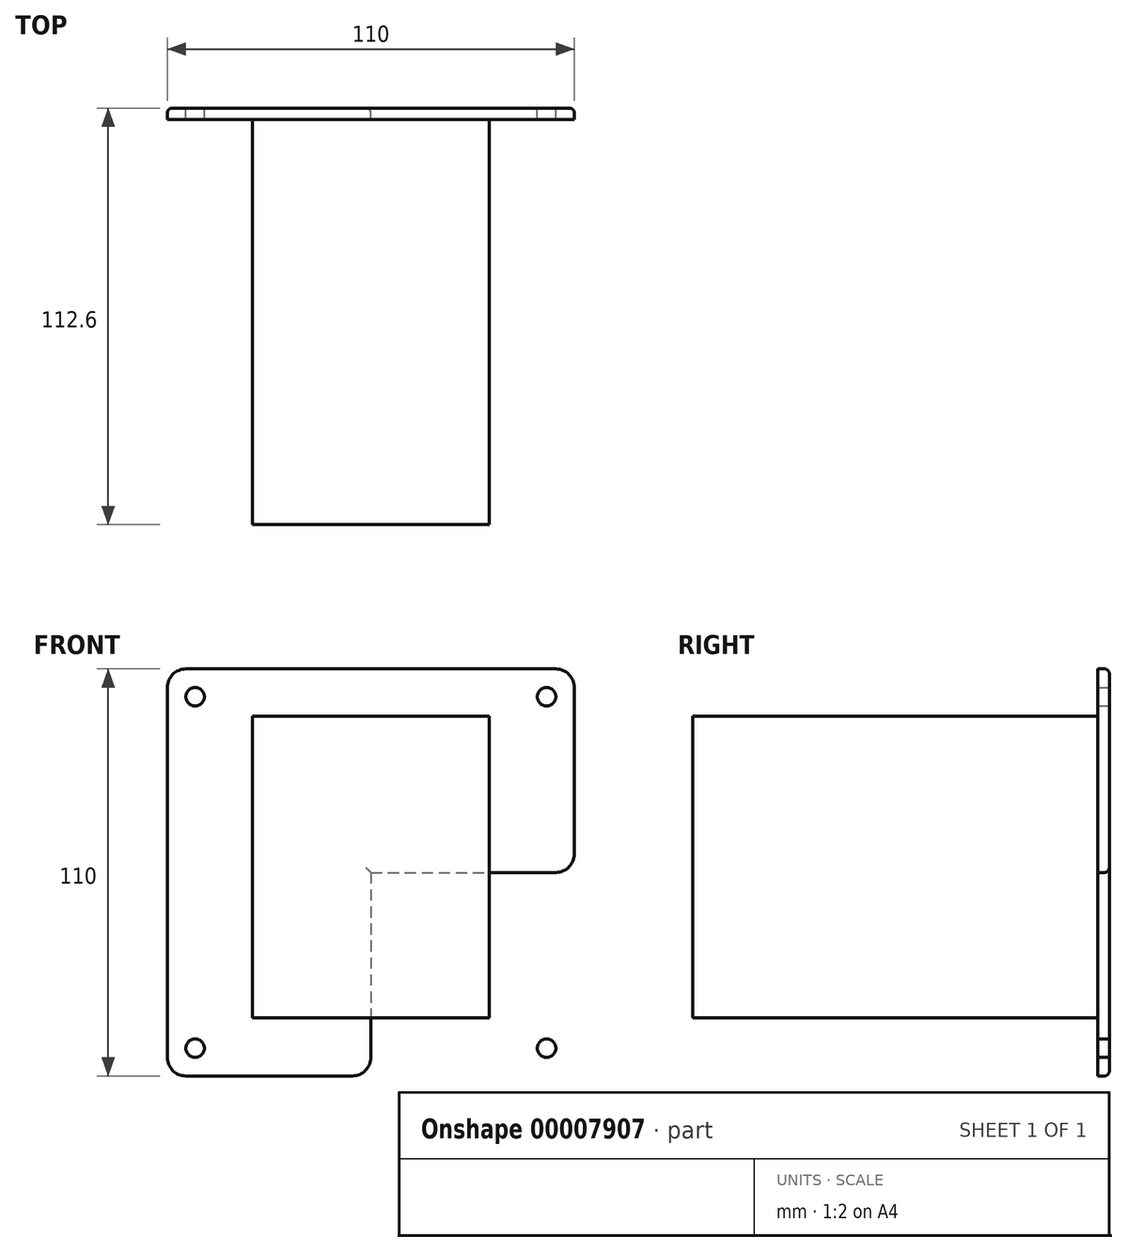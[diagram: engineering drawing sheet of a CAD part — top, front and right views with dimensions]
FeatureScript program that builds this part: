
annotation { "Feature Type Name" : "Feature", "Feature Type Description" : "" }
export const myFeature = defineFeature(function(context is Context, id is Id, definition is map)
    precondition{}
    {
        {
            var Q0;
            Q0=qCreatedBy(makeId("Front.planeOp"),FACE);
            var sketch = newSketch(context, id + "F0", { "sketchPlane" : qUnion([Q0])});
            skLineSegment(sketch, "E0.bottom", {"start": v(-55, 53.55) * mm, "end": v(55, 53.55) * mm});
            skLineSegment(sketch, "E0.top", {"start": v(-55, -56.45) * mm, "end": v(55, -56.45) * mm});
            skLineSegment(sketch, "E0.left", {"start": v(-55, 53.55) * mm, "end": v(-55, -56.45) * mm});
            skLineSegment(sketch, "E0.right", {"start": v(55, 53.55) * mm, "end": v(55, -56.45) * mm});
            skCircle(sketch, "E1", {"center": v(-47.5, 46.05) * mm, "radius": 2.5 * mm});
            skCircle(sketch, "E2", {"center": v(-47.5, -48.95) * mm, "radius": 2.5 * mm});
            skPoint(sketch, "E3", {"position": v(84.62, 69.4) * mm});
            skCircle(sketch, "E4.0.MirrorC", {"center": v(47.5, -48.95) * mm, "radius": 2.5 * mm});
            skCircle(sketch, "E4.1.MirrorC", {"center": v(47.5, 46.05) * mm, "radius": 2.5 * mm});
            skPoint(sketch, "E5", {"position": v(0, 53.55) * mm});
            skPoint(sketch, "E6", {"position": v(0, -56.45) * mm});
            skPoint(sketch, "E7", {"position": v(-55, -1.45) * mm});
            skPoint(sketch, "E8", {"position": v(55, -1.45) * mm});
            skLineSegment(sketch, "E9", {"start": v(0, 53.55) * mm, "end": v(0, -56.45) * mm});
            skLineSegment(sketch, "E10", {"start": v(-55, -1.45) * mm, "end": v(55, -1.45) * mm});
            skSolve(sketch);
        }
        {
            var Q0;
            Q0=makeQuery(id+"F0.imprint","IMPRINT",FACE,{"disambiguationData":[TD([[makeQuery(id+"F0.imprint","IMPRINT",EDGE,{"derivedFrom":sQuery(id+"F0.wireOp",EDGE,"E0.bottom")}),-1.0]])]});
            var Q1;
            Q1=makeQuery(id+"F0.imprint","IMPRINT",FACE,{"disambiguationData":[TD([[makeQuery(id+"F0.imprint","IMPRINT",EDGE,{"derivedFrom":sQuery(id+"F0.wireOp",EDGE,"E2")}),-1.0]])]});
            var Q2;
            Q2=makeQuery(id+"F0.imprint","IMPRINT",FACE,{"disambiguationData":[TD([[makeQuery(id+"F0.imprint","IMPRINT",EDGE,{"derivedFrom":sQuery(id+"F0.wireOp",EDGE,"E4.0.MirrorC")}),1.0]])]});
            extrude(context, id + "F1", {"entities" : qUnion([Q0, Q1, Q2]), "depth" : 3.1 * mm});
        }
        {
            var Q0;
            Q0=makeQuery(id+"F1.opExtrude","SWEPT_EDGE",EDGE,{"disambiguationData":[OSD([sQuery(id+"F0.wireOp",EDGE,"E0.bottom"),sQuery(id+"F0.wireOp",EDGE,"E0.right")])]});
            var Q1;
            Q1=makeQuery(id+"F1.opExtrude","SWEPT_EDGE",EDGE,{"disambiguationData":[OSD([sQuery(id+"F0.wireOp",EDGE,"E0.bottom"),sQuery(id+"F0.wireOp",EDGE,"E0.left")])]});
            var Q2;
            Q2=makeQuery(id+"F1.opExtrude","SWEPT_EDGE",EDGE,{"disambiguationData":[OSD([sQuery(id+"F0.wireOp",EDGE,"E0.top"),sQuery(id+"F0.wireOp",EDGE,"E0.left")])]});
            var Q3;
            Q3=makeQuery(id+"F1.opExtrude","SWEPT_EDGE",EDGE,{"disambiguationData":[OSD([sQuery(id+"F0.wireOp",EDGE,"E0.top"),sQuery(id+"F0.wireOp",EDGE,"E0.right")])]});
            fillet(context, id + "F2", {"entities" : qUnion([Q0, Q1, Q2, Q3]), "radius" : 5 * mm, "tangentPropagation" : true, "allowEdgeOverflow" : false});
        }
        {
            var Q0;
            Q0=makeQuery(id+"F1.opExtrude","CAP_FACE",FACE,{"disambiguationData":[OSD([sQuery(id+"F0.wireOp",EDGE,"E0.bottom"),sQuery(id+"F0.wireOp",EDGE,"E0.top"),sQuery(id+"F0.wireOp",EDGE,"E0.left"),sQuery(id+"F0.wireOp",EDGE,"E0.right"),sQuery(id+"F0.wireOp",EDGE,"E1"),sQuery(id+"F0.wireOp",EDGE,"E2"),sQuery(id+"F0.wireOp",EDGE,"E4.0.MirrorC"),sQuery(id+"F0.wireOp",EDGE,"E4.1.MirrorC")])],"isStart":false});
            var sketch = newSketch(context, id + "F3", { "sketchPlane" : qUnion([Q0])});
            skLineSegment(sketch, "E11.bottom", {"start": v(-32, 40.75) * mm, "end": v(32, 40.75) * mm});
            skLineSegment(sketch, "E11.top", {"start": v(-32, -40.75) * mm, "end": v(32, -40.75) * mm});
            skLineSegment(sketch, "E11.left", {"start": v(-32, 40.75) * mm, "end": v(-32, -40.75) * mm});
            skLineSegment(sketch, "E11.right", {"start": v(32, 40.75) * mm, "end": v(32, -40.75) * mm});
            skPoint(sketch, "E12", {"position": v(0, 40.75) * mm});
            skPoint(sketch, "E13", {"position": v(-32, 0) * mm});
            skLineSegment(sketch, "E14", {"start": v(0, 40.75) * mm, "end": v(0, 0) * mm});
            skLineSegment(sketch, "E15", {"start": v(0, 0) * mm, "end": v(-32, 0) * mm});
            skSolve(sketch);
        }
        {
            var Q0;
            {var subQ0=sQuery(id+"F3.wireOp",EDGE,"E14");Q0=makeQuery(id+"F3.imprint","IMPRINT",FACE,{"disambiguationData":[TD([[makeQuery(id+"F3.imprint","IMPRINT",EDGE,{"derivedFrom":subQ0}),-1.0]])]});}
            var Q1;
            {var subQ4=sQuery(id+"F3.wireOp",EDGE,"E11.top");Q1=makeQuery(id+"F3.imprint","IMPRINT",FACE,{"disambiguationData":[TD([[makeQuery(id+"F3.imprint","IMPRINT",EDGE,{"derivedFrom":subQ4}),1.0]])]});}
            extrude(context, id + "F4", {"entities" : qUnion([Q0, Q1]), "depth" : 109.5 * mm});
        }
        {
            var Q0;
            Q0=makeQuery(id+"F1.opExtrude","CAP_EDGE",EDGE,{"disambiguationData":[OSD([sQuery(id+"F0.wireOp",EDGE,"E0.bottom")])],"isStart":true});
            var Q1;
            {var subQ0=sQuery(id+"F0.wireOp",EDGE,"E0.right");var subQ1=sQuery(id+"F0.wireOp",EDGE,"E0.bottom");Q1=makeQuery(id+"F2.opFillet","BLEND_EDGE",EDGE,{"blendedFrom":[makeQuery(id+"F1.opExtrude","SWEPT_EDGE",EDGE,{"disambiguationData":[OSD([subQ1,subQ0])]}),makeQuery(id+"F1.opExtrude","CAP_FACE",FACE,{"disambiguationData":[OSD([subQ1,sQuery(id+"F0.wireOp",EDGE,"E0.top"),sQuery(id+"F0.wireOp",EDGE,"E0.left"),subQ0,sQuery(id+"F0.wireOp",EDGE,"E1"),sQuery(id+"F0.wireOp",EDGE,"E2"),sQuery(id+"F0.wireOp",EDGE,"E4.0.MirrorC"),sQuery(id+"F0.wireOp",EDGE,"E4.1.MirrorC")])],"isStart":true})],"blendedInto":[makeQuery(id+"F1.opExtrude","CAP_FACE",FACE,{"disambiguationData":[OSD([subQ1,sQuery(id+"F0.wireOp",EDGE,"E0.top"),sQuery(id+"F0.wireOp",EDGE,"E0.left"),subQ0,sQuery(id+"F0.wireOp",EDGE,"E1"),sQuery(id+"F0.wireOp",EDGE,"E2"),sQuery(id+"F0.wireOp",EDGE,"E4.0.MirrorC"),sQuery(id+"F0.wireOp",EDGE,"E4.1.MirrorC")])],"isStart":true})]});}
            var Q2;
            Q2=makeQuery(id+"F1.opExtrude","CAP_EDGE",EDGE,{"disambiguationData":[OSD([sQuery(id+"F0.wireOp",EDGE,"E0.right")])],"isStart":true});
            var Q3;
            {var subQ0=sQuery(id+"F0.wireOp",EDGE,"E0.right");var subQ1=sQuery(id+"F0.wireOp",EDGE,"E0.top");Q3=makeQuery(id+"F2.opFillet","BLEND_EDGE",EDGE,{"blendedFrom":[makeQuery(id+"F1.opExtrude","SWEPT_EDGE",EDGE,{"disambiguationData":[OSD([subQ1,subQ0])]}),makeQuery(id+"F1.opExtrude","CAP_FACE",FACE,{"disambiguationData":[OSD([sQuery(id+"F0.wireOp",EDGE,"E0.bottom"),subQ1,sQuery(id+"F0.wireOp",EDGE,"E0.left"),subQ0,sQuery(id+"F0.wireOp",EDGE,"E1"),sQuery(id+"F0.wireOp",EDGE,"E2"),sQuery(id+"F0.wireOp",EDGE,"E4.0.MirrorC"),sQuery(id+"F0.wireOp",EDGE,"E4.1.MirrorC")])],"isStart":true})],"blendedInto":[makeQuery(id+"F1.opExtrude","CAP_FACE",FACE,{"disambiguationData":[OSD([sQuery(id+"F0.wireOp",EDGE,"E0.bottom"),subQ1,sQuery(id+"F0.wireOp",EDGE,"E0.left"),subQ0,sQuery(id+"F0.wireOp",EDGE,"E1"),sQuery(id+"F0.wireOp",EDGE,"E2"),sQuery(id+"F0.wireOp",EDGE,"E4.0.MirrorC"),sQuery(id+"F0.wireOp",EDGE,"E4.1.MirrorC")])],"isStart":true})]});}
            var Q4;
            Q4=makeQuery(id+"F1.opExtrude","CAP_EDGE",EDGE,{"disambiguationData":[OSD([sQuery(id+"F0.wireOp",EDGE,"E0.top")])],"isStart":true});
            var Q5;
            {var subQ0=sQuery(id+"F0.wireOp",EDGE,"E0.left");var subQ1=sQuery(id+"F0.wireOp",EDGE,"E0.top");Q5=makeQuery(id+"F2.opFillet","BLEND_EDGE",EDGE,{"blendedFrom":[makeQuery(id+"F1.opExtrude","SWEPT_EDGE",EDGE,{"disambiguationData":[OSD([subQ1,subQ0])]}),makeQuery(id+"F1.opExtrude","CAP_FACE",FACE,{"disambiguationData":[OSD([sQuery(id+"F0.wireOp",EDGE,"E0.bottom"),subQ1,subQ0,sQuery(id+"F0.wireOp",EDGE,"E0.right"),sQuery(id+"F0.wireOp",EDGE,"E1"),sQuery(id+"F0.wireOp",EDGE,"E2"),sQuery(id+"F0.wireOp",EDGE,"E4.0.MirrorC"),sQuery(id+"F0.wireOp",EDGE,"E4.1.MirrorC")])],"isStart":true})],"blendedInto":[makeQuery(id+"F1.opExtrude","CAP_FACE",FACE,{"disambiguationData":[OSD([sQuery(id+"F0.wireOp",EDGE,"E0.bottom"),subQ1,subQ0,sQuery(id+"F0.wireOp",EDGE,"E0.right"),sQuery(id+"F0.wireOp",EDGE,"E1"),sQuery(id+"F0.wireOp",EDGE,"E2"),sQuery(id+"F0.wireOp",EDGE,"E4.0.MirrorC"),sQuery(id+"F0.wireOp",EDGE,"E4.1.MirrorC")])],"isStart":true})]});}
            var Q6;
            Q6=makeQuery(id+"F1.opExtrude","CAP_EDGE",EDGE,{"disambiguationData":[OSD([sQuery(id+"F0.wireOp",EDGE,"E0.left")])],"isStart":true});
            var Q7;
            {var subQ0=sQuery(id+"F0.wireOp",EDGE,"E0.left");var subQ1=sQuery(id+"F0.wireOp",EDGE,"E0.bottom");Q7=makeQuery(id+"F2.opFillet","BLEND_EDGE",EDGE,{"blendedFrom":[makeQuery(id+"F1.opExtrude","SWEPT_EDGE",EDGE,{"disambiguationData":[OSD([subQ1,subQ0])]}),makeQuery(id+"F1.opExtrude","CAP_FACE",FACE,{"disambiguationData":[OSD([subQ1,sQuery(id+"F0.wireOp",EDGE,"E0.top"),subQ0,sQuery(id+"F0.wireOp",EDGE,"E0.right"),sQuery(id+"F0.wireOp",EDGE,"E1"),sQuery(id+"F0.wireOp",EDGE,"E2"),sQuery(id+"F0.wireOp",EDGE,"E4.0.MirrorC"),sQuery(id+"F0.wireOp",EDGE,"E4.1.MirrorC")])],"isStart":true})],"blendedInto":[makeQuery(id+"F1.opExtrude","CAP_FACE",FACE,{"disambiguationData":[OSD([subQ1,sQuery(id+"F0.wireOp",EDGE,"E0.top"),subQ0,sQuery(id+"F0.wireOp",EDGE,"E0.right"),sQuery(id+"F0.wireOp",EDGE,"E1"),sQuery(id+"F0.wireOp",EDGE,"E2"),sQuery(id+"F0.wireOp",EDGE,"E4.0.MirrorC"),sQuery(id+"F0.wireOp",EDGE,"E4.1.MirrorC")])],"isStart":true})]});}
            fillet(context, id + "F5", {"entities" : qUnion([Q0, Q1, Q2, Q3, Q4, Q5, Q6, Q7]), "radius" : 1.27 * mm, "tangentPropagation" : true, "allowEdgeOverflow" : false});
        }
    });
